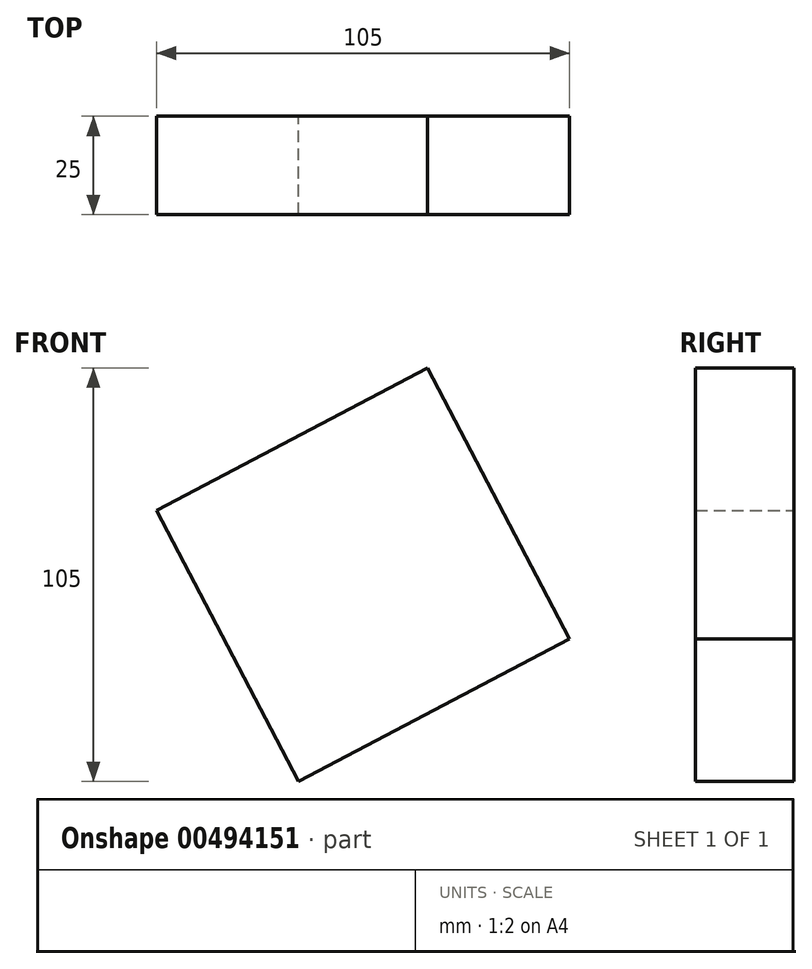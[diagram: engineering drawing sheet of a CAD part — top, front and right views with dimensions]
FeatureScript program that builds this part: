
annotation { "Feature Type Name" : "Feature", "Feature Type Description" : "" }
export const myFeature = defineFeature(function(context is Context, id is Id, definition is map)
    precondition{}
    {
        {
            var Q0;
            Q0=qCreatedBy(makeId("Front.planeOp"),FACE);
            var sketch = newSketch(context, id + "F0", { "sketchPlane" : qUnion([Q0])});
            skCircle(sketch, "E0.cCircle", {"center": v(-2.58, 5.88) * mm, "radius": 38.88 * mm, "construction": true});
            skLineSegment(sketch, "E0.0", {"start": v(49.92, -10.47) * mm, "end": v(-18.93, -46.62) * mm});
            skLineSegment(sketch, "E0.1", {"start": v(-18.93, -46.62) * mm, "end": v(-55.08, 22.23) * mm});
            skLineSegment(sketch, "E0.2", {"start": v(-55.08, 22.23) * mm, "end": v(13.77, 58.38) * mm});
            skLineSegment(sketch, "E0.3", {"start": v(13.77, 58.38) * mm, "end": v(49.92, -10.47) * mm});
            skPoint(sketch, "E0.0.midPoint", {"position": v(15.5, -28.55) * mm});
            skSolve(sketch);
        }
        {
            var Q0;
            Q0=makeQuery(id+"F0.imprint","IMPRINT",FACE,{"disambiguationData":[TD([[makeQuery(id+"F0.imprint","IMPRINT",EDGE,{"derivedFrom":sQuery(id+"F0.wireOp",EDGE,"E0.0")}),-1.0]])]});
            extrude(context, id + "F1", {"entities" : qUnion([Q0]), "depth" : 25 * mm});
        }
    });
